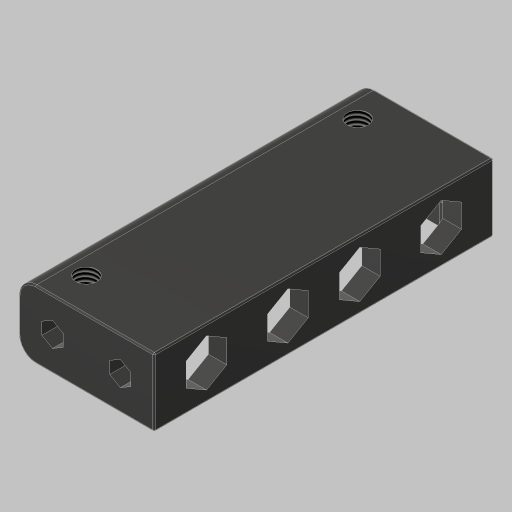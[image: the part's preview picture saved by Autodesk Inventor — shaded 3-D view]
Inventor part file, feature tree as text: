
AUTODESK INVENTOR PART (.ipt)
format: ipt  version: 2023.5 (Build 275446000, 446)  size: 369,152 bytes
history: native  units: in
note: dims shown in document units (in); Inventor stores cm internally (conversion verified against a paired STEP export)
features: sketch x5, extrude x4, fillet x3, projected_geometry x2, hole x1
ambient origin geometry x8: Origin, YZ Plane, XZ Plane, XY Plane, X Axis, Y Axis, Z Axis, Center Point
bodies: Solid1 (feature_tree)
feature tree (15):
  extrude  "Extrusion1"  Depth=0.5in
  hole  "Hole1"  [1 undecoded]
  fillet  "Fillet1"  Radius=0.25in
  fillet  "Fillet2"  Radius=0.125in
  extrude  "Extrusion2"  Depth=0.125in
  fillet  "Fillet3"  Radius=0.125in
  extrude  "Extrusion3"  Depth=0.375in TaperAngle=0.0deg
  extrude  "Extrusion4"  Depth=0.13in
  sketch  "Sketch1"  dims[d0=1.0in d1=0.5in]
  sketch  "Sketch2"  dims[d2=2.5in d3=0.0in d4=2.0in d5=0.25in]
  sketch  "Sketch3"  dims[d6=0.156in d7=0.38in d8=0.385in d9=0.25in d10=0.5635in d11=1.0in d12=0.8108in d13=0.125in]
  sketch  "Sketch4"  dims[d14=0.01in d15=0.125in d16=0.125in]
  sketch  "Sketch5"  dims[d17=0.125in d18=0.375in d19=0.0in d20=0.13in d21=0.3in d22=0.375in d23=0.7874in d25=0.6in d26=0.3937in d28=1.0in d30=0.0in d31=0.0in d32=0.25in d33=0.0in d34=0.0in]
  projected_geometry  "Project Cut Edges1"
  projected_geometry  "Project Cut Edges2"
note: 1 required parameter value undecoded (feature->parameter linkage not recoverable at this tier; creation-order binding heuristic only, values carry confidence <= 0.55)
